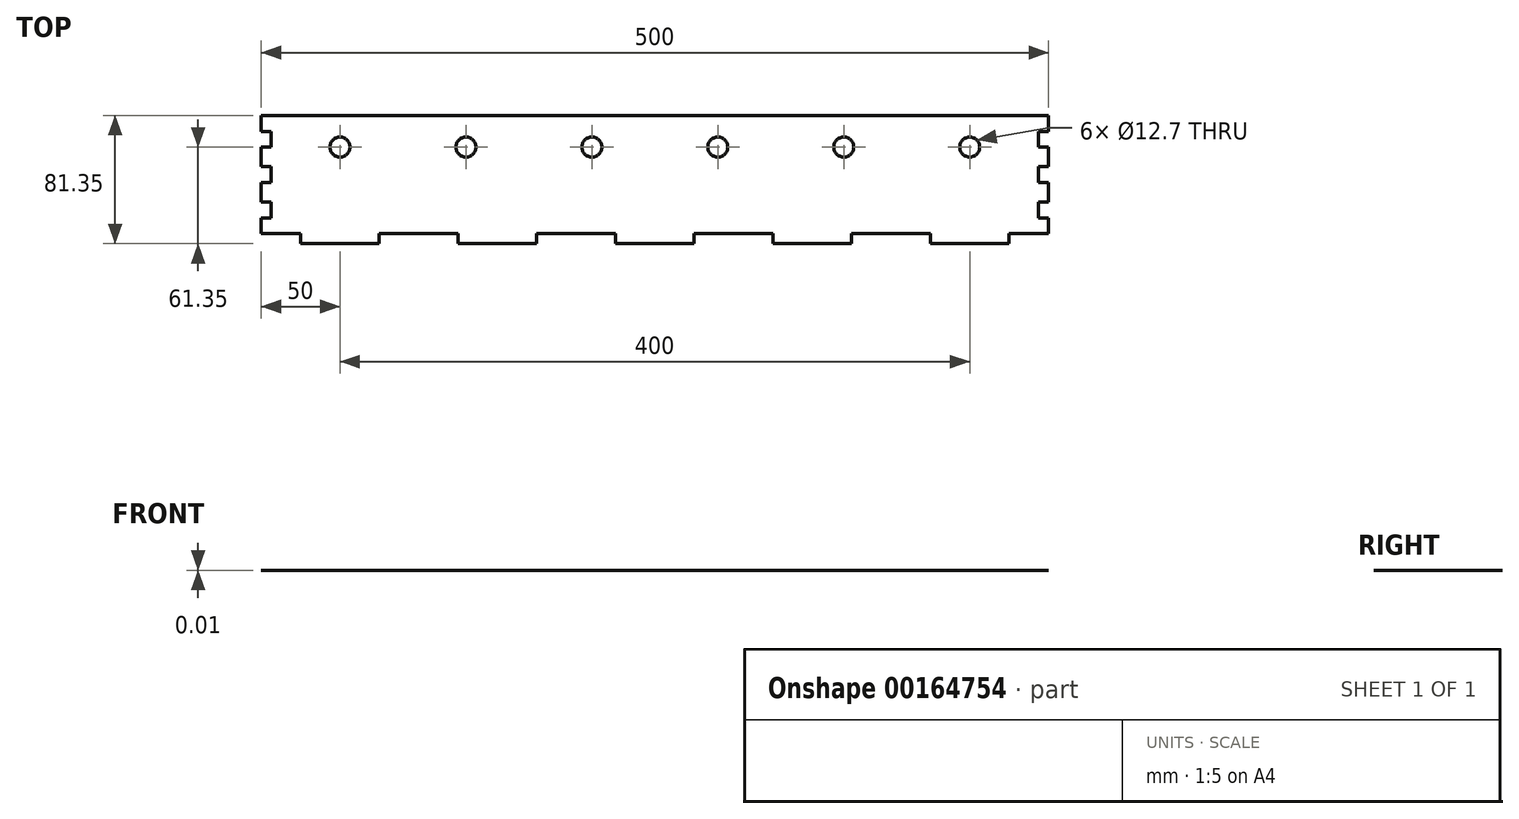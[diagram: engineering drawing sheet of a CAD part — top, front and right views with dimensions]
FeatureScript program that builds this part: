
annotation { "Feature Type Name" : "Feature", "Feature Type Description" : "" }
export const myFeature = defineFeature(function(context is Context, id is Id, definition is map)
    precondition{}
    {
        {
            var Q0;
            Q0=qCreatedBy(makeId("Top.planeOp"),FACE);
            var sketch = newSketch(context, id + "F0", { "sketchPlane" : qUnion([Q0])});
            skLineSegment(sketch, "E0.bottom", {"start": v(-250, 37.5) * mm, "end": v(250, 37.5) * mm});
            skLineSegment(sketch, "E0.top", {"start": v(-250, -37.5) * mm, "end": v(250, -37.5) * mm});
            skLineSegment(sketch, "E0.left", {"start": v(-250, 37.5) * mm, "end": v(-250, -37.5) * mm});
            skLineSegment(sketch, "E0.right", {"start": v(250, 37.5) * mm, "end": v(250, -37.5) * mm});
            skPoint(sketch, "E0.middle", {"position": v(0, 0) * mm});
            skSolve(sketch);
        }
        {
            var Q0;
            Q0=qSketchRegion(id+"F0",true);
            extrude(context, id + "F1", {"entities" : qUnion([Q0]), "depth" : 1 / 101.6 * mm});
        }
        {
            var Q0;
            Q0=makeQuery(id+"F1.opExtrude","CAP_FACE",FACE,{"disambiguationData":[OSD([sQuery(id+"F0.wireOp",EDGE,"E0.bottom"),sQuery(id+"F0.wireOp",EDGE,"E0.top"),sQuery(id+"F0.wireOp",EDGE,"E0.left"),sQuery(id+"F0.wireOp",EDGE,"E0.right")])],"isStart":false});
            var sketch = newSketch(context, id + "F2", { "sketchPlane" : qUnion([Q0])});
            skLineSegment(sketch, "E1.bottom", {"start": v(-225, 37.5) * mm, "end": v(-175, 37.5) * mm, "construction": true});
            skLineSegment(sketch, "E1.top", {"start": v(-225, 31.15) * mm, "end": v(-175, 31.15) * mm, "construction": true});
            skLineSegment(sketch, "E1.left", {"start": v(-225, 37.5) * mm, "end": v(-225, 31.15) * mm, "construction": true});
            skLineSegment(sketch, "E1.right", {"start": v(-175, 37.5) * mm, "end": v(-175, 31.15) * mm, "construction": true});
            skLineSegment(sketch, "E2.0.1.0", {"start": v(-225, -37.5) * mm, "end": v(-175, -37.5) * mm});
            skLineSegment(sketch, "E2.0.1.1", {"start": v(-225, -43.85) * mm, "end": v(-175, -43.85) * mm});
            skLineSegment(sketch, "E2.0.1.2", {"start": v(-225, -37.5) * mm, "end": v(-225, -43.85) * mm});
            skLineSegment(sketch, "E2.0.1.3", {"start": v(-175, -37.5) * mm, "end": v(-175, -43.85) * mm});
            skLineSegment(sketch, "E2.1.0.0", {"start": v(-125, 37.5) * mm, "end": v(-75, 37.5) * mm, "construction": true});
            skLineSegment(sketch, "E2.1.0.1", {"start": v(-125, 31.15) * mm, "end": v(-75, 31.15) * mm, "construction": true});
            skLineSegment(sketch, "E2.1.0.2", {"start": v(-125, 37.5) * mm, "end": v(-125, 31.15) * mm, "construction": true});
            skLineSegment(sketch, "E2.1.0.3", {"start": v(-75, 37.5) * mm, "end": v(-75, 31.15) * mm, "construction": true});
            skLineSegment(sketch, "E2.1.1.0", {"start": v(-125, -37.5) * mm, "end": v(-75, -37.5) * mm});
            skLineSegment(sketch, "E2.1.1.1", {"start": v(-125, -43.85) * mm, "end": v(-75, -43.85) * mm});
            skLineSegment(sketch, "E2.1.1.2", {"start": v(-125, -37.5) * mm, "end": v(-125, -43.85) * mm});
            skLineSegment(sketch, "E2.1.1.3", {"start": v(-75, -37.5) * mm, "end": v(-75, -43.85) * mm});
            skLineSegment(sketch, "E2.2.0.0", {"start": v(-25, 37.5) * mm, "end": v(25, 37.5) * mm, "construction": true});
            skLineSegment(sketch, "E2.2.0.1", {"start": v(-25, 31.15) * mm, "end": v(25, 31.15) * mm, "construction": true});
            skLineSegment(sketch, "E2.2.0.2", {"start": v(-25, 37.5) * mm, "end": v(-25, 31.15) * mm, "construction": true});
            skLineSegment(sketch, "E2.2.0.3", {"start": v(25, 37.5) * mm, "end": v(25, 31.15) * mm, "construction": true});
            skLineSegment(sketch, "E2.2.1.0", {"start": v(-25, -37.5) * mm, "end": v(25, -37.5) * mm});
            skLineSegment(sketch, "E2.2.1.1", {"start": v(-25, -43.85) * mm, "end": v(25, -43.85) * mm});
            skLineSegment(sketch, "E2.2.1.2", {"start": v(-25, -37.5) * mm, "end": v(-25, -43.85) * mm});
            skLineSegment(sketch, "E2.2.1.3", {"start": v(25, -37.5) * mm, "end": v(25, -43.85) * mm});
            skLineSegment(sketch, "E2.3.0.0", {"start": v(75, 37.5) * mm, "end": v(125, 37.5) * mm, "construction": true});
            skLineSegment(sketch, "E2.3.0.1", {"start": v(75, 31.15) * mm, "end": v(125, 31.15) * mm, "construction": true});
            skLineSegment(sketch, "E2.3.0.2", {"start": v(75, 37.5) * mm, "end": v(75, 31.15) * mm, "construction": true});
            skLineSegment(sketch, "E2.3.0.3", {"start": v(125, 37.5) * mm, "end": v(125, 31.15) * mm, "construction": true});
            skLineSegment(sketch, "E2.3.1.0", {"start": v(75, -37.5) * mm, "end": v(125, -37.5) * mm});
            skLineSegment(sketch, "E2.3.1.1", {"start": v(75, -43.85) * mm, "end": v(125, -43.85) * mm});
            skLineSegment(sketch, "E2.3.1.2", {"start": v(75, -37.5) * mm, "end": v(75, -43.85) * mm});
            skLineSegment(sketch, "E2.3.1.3", {"start": v(125, -37.5) * mm, "end": v(125, -43.85) * mm});
            skLineSegment(sketch, "E2.4.0.0", {"start": v(175, 37.5) * mm, "end": v(225, 37.5) * mm, "construction": true});
            skLineSegment(sketch, "E2.4.0.1", {"start": v(175, 31.15) * mm, "end": v(225, 31.15) * mm, "construction": true});
            skLineSegment(sketch, "E2.4.0.2", {"start": v(175, 37.5) * mm, "end": v(175, 31.15) * mm, "construction": true});
            skLineSegment(sketch, "E2.4.0.3", {"start": v(225, 37.5) * mm, "end": v(225, 31.15) * mm, "construction": true});
            skLineSegment(sketch, "E2.4.1.0", {"start": v(175, -37.5) * mm, "end": v(225, -37.5) * mm});
            skLineSegment(sketch, "E2.4.1.1", {"start": v(175, -43.85) * mm, "end": v(225, -43.85) * mm});
            skLineSegment(sketch, "E2.4.1.2", {"start": v(175, -37.5) * mm, "end": v(175, -43.85) * mm});
            skLineSegment(sketch, "E2.4.1.3", {"start": v(225, -37.5) * mm, "end": v(225, -43.85) * mm});
            skLineSegment(sketch, "E2.direction1", {"start": v(-225, 31.15) * mm, "end": v(-125, 31.15) * mm, "construction": true});
            skLineSegment(sketch, "E2.direction2", {"start": v(-225, 31.15) * mm, "end": v(-225, -43.85) * mm, "construction": true});
            skLineSegment(sketch, "E3.bottom", {"start": v(250, 27.5) * mm, "end": v(243.65, 27.5) * mm, "construction": true});
            skLineSegment(sketch, "E3.top", {"start": v(250, 17.5) * mm, "end": v(243.65, 17.5) * mm, "construction": true});
            skLineSegment(sketch, "E3.left", {"start": v(250, 27.5) * mm, "end": v(250, 17.5) * mm, "construction": true});
            skLineSegment(sketch, "E3.right", {"start": v(243.65, 27.5) * mm, "end": v(243.65, 17.5) * mm, "construction": true});
            skLineSegment(sketch, "E4.0.1.0", {"start": v(243.65, 5) * mm, "end": v(243.65, -5) * mm, "construction": true});
            skLineSegment(sketch, "E4.0.1.1", {"start": v(250, 5) * mm, "end": v(250, -5) * mm, "construction": true});
            skLineSegment(sketch, "E4.0.1.2", {"start": v(250, 5) * mm, "end": v(243.65, 5) * mm, "construction": true});
            skLineSegment(sketch, "E4.0.1.3", {"start": v(250, -5) * mm, "end": v(243.65, -5) * mm, "construction": true});
            skLineSegment(sketch, "E4.direction1", {"start": v(243.65, 17.5) * mm, "end": v(243.65, 17.5) * mm});
            skLineSegment(sketch, "E4.direction2", {"start": v(243.65, 17.5) * mm, "end": v(243.65, 5) * mm, "construction": true});
            skLineSegment(sketch, "E5.0.0.2", {"start": v(243.65, -17.5) * mm, "end": v(243.65, -27.5) * mm, "construction": true});
            skLineSegment(sketch, "E5.3.0.2", {"start": v(250, -17.5) * mm, "end": v(250, -27.5) * mm, "construction": true});
            skLineSegment(sketch, "E5.6.0.2", {"start": v(250, -17.5) * mm, "end": v(243.65, -17.5) * mm, "construction": true});
            skLineSegment(sketch, "E5.9.0.2", {"start": v(250, -27.5) * mm, "end": v(243.65, -27.5) * mm, "construction": true});
            skSolve(sketch);
        }
        {
            var Q0;
            Q0=qSketchRegion(id+"F2",true);
            var Q1;
            Q1=makeQuery(id+"F1.opExtrude","CAP_FACE",FACE,{"disambiguationData":[OSD([sQuery(id+"F0.wireOp",EDGE,"E0.bottom"),sQuery(id+"F0.wireOp",EDGE,"E0.top"),sQuery(id+"F0.wireOp",EDGE,"E0.left"),sQuery(id+"F0.wireOp",EDGE,"E0.right")])],"isStart":true});
            extrude(context, id + "F3", {"entities" : qUnion([Q0]), "operationType" : NewBodyOperationType.ADD, "endBound" : BoundingType.UP_TO_SURFACE, "oppositeDirection" : true, "endBoundEntityFace" : qUnion([Q1]), "depth" : 25 * mm});
        }
        {
            var Q0;
            Q0=makeQuery(id+"F3.boolean.opBoolean","MERGE",FACE,{"derivedFrom":[makeQuery(id+"F1.opExtrude","CAP_FACE",FACE,{"disambiguationData":[OSD([sQuery(id+"F0.wireOp",EDGE,"E0.bottom"),sQuery(id+"F0.wireOp",EDGE,"E0.top"),sQuery(id+"F0.wireOp",EDGE,"E0.left"),sQuery(id+"F0.wireOp",EDGE,"E0.right")])],"isStart":false}),makeQuery(id+"F3.opExtrude","CAP_FACE",FACE,{"disambiguationData":[OSD([sQuery(id+"F2.wireOp",EDGE,"E2.0.1.0"),sQuery(id+"F2.wireOp",EDGE,"E2.0.1.1"),sQuery(id+"F2.wireOp",EDGE,"E2.0.1.2"),sQuery(id+"F2.wireOp",EDGE,"E2.0.1.3")])],"isStart":true}),makeQuery(id+"F3.opExtrude","CAP_FACE",FACE,{"disambiguationData":[OSD([sQuery(id+"F2.wireOp",EDGE,"E2.1.1.0"),sQuery(id+"F2.wireOp",EDGE,"E2.1.1.1"),sQuery(id+"F2.wireOp",EDGE,"E2.1.1.2"),sQuery(id+"F2.wireOp",EDGE,"E2.1.1.3")])],"isStart":true}),makeQuery(id+"F3.opExtrude","CAP_FACE",FACE,{"disambiguationData":[OSD([sQuery(id+"F2.wireOp",EDGE,"E2.2.1.0"),sQuery(id+"F2.wireOp",EDGE,"E2.2.1.1"),sQuery(id+"F2.wireOp",EDGE,"E2.2.1.2"),sQuery(id+"F2.wireOp",EDGE,"E2.2.1.3")])],"isStart":true}),makeQuery(id+"F3.opExtrude","CAP_FACE",FACE,{"disambiguationData":[OSD([sQuery(id+"F2.wireOp",EDGE,"E2.3.1.0"),sQuery(id+"F2.wireOp",EDGE,"E2.3.1.1"),sQuery(id+"F2.wireOp",EDGE,"E2.3.1.2"),sQuery(id+"F2.wireOp",EDGE,"E2.3.1.3")])],"isStart":true}),makeQuery(id+"F3.opExtrude","CAP_FACE",FACE,{"disambiguationData":[OSD([sQuery(id+"F2.wireOp",EDGE,"E2.4.1.0"),sQuery(id+"F2.wireOp",EDGE,"E2.4.1.1"),sQuery(id+"F2.wireOp",EDGE,"E2.4.1.2"),sQuery(id+"F2.wireOp",EDGE,"E2.4.1.3")])],"isStart":true})]});
            var sketch = newSketch(context, id + "F4", { "sketchPlane" : qUnion([Q0])});
            skLineSegment(sketch, "E6", {"start": v(243.65, 27.5) * mm, "end": v(243.65, 17.5) * mm});
            skLineSegment(sketch, "E7", {"start": v(243.65, 17.5) * mm, "end": v(250, 17.5) * mm});
            skLineSegment(sketch, "E8", {"start": v(250, 17.5) * mm, "end": v(250, 27.5) * mm});
            skLineSegment(sketch, "E9", {"start": v(250, 27.5) * mm, "end": v(243.65, 27.5) * mm});
            skLineSegment(sketch, "E10.0.1.0", {"start": v(250, 5) * mm, "end": v(243.65, 5) * mm});
            skLineSegment(sketch, "E10.0.1.1", {"start": v(243.65, -5) * mm, "end": v(250, -5) * mm});
            skLineSegment(sketch, "E10.0.1.2", {"start": v(250, -5) * mm, "end": v(250, 5) * mm});
            skLineSegment(sketch, "E10.0.1.3", {"start": v(243.65, 5) * mm, "end": v(243.65, -5) * mm});
            skLineSegment(sketch, "E10.0.2.0", {"start": v(250, -17.5) * mm, "end": v(243.65, -17.5) * mm});
            skLineSegment(sketch, "E10.0.2.1", {"start": v(243.65, -27.5) * mm, "end": v(250, -27.5) * mm});
            skLineSegment(sketch, "E10.0.2.2", {"start": v(250, -27.5) * mm, "end": v(250, -17.5) * mm});
            skLineSegment(sketch, "E10.0.2.3", {"start": v(243.65, -17.5) * mm, "end": v(243.65, -27.5) * mm});
            skLineSegment(sketch, "E10.1.0.0", {"start": v(-243.65, 27.5) * mm, "end": v(-250, 27.5) * mm});
            skLineSegment(sketch, "E10.1.0.1", {"start": v(-250, 17.5) * mm, "end": v(-243.65, 17.5) * mm});
            skLineSegment(sketch, "E10.1.0.2", {"start": v(-243.65, 17.5) * mm, "end": v(-243.65, 27.5) * mm});
            skLineSegment(sketch, "E10.1.0.3", {"start": v(-250, 27.5) * mm, "end": v(-250, 17.5) * mm});
            skLineSegment(sketch, "E10.1.1.0", {"start": v(-243.65, 5) * mm, "end": v(-250, 5) * mm});
            skLineSegment(sketch, "E10.1.1.1", {"start": v(-250, -5) * mm, "end": v(-243.65, -5) * mm});
            skLineSegment(sketch, "E10.1.1.2", {"start": v(-243.65, -5) * mm, "end": v(-243.65, 5) * mm});
            skLineSegment(sketch, "E10.1.1.3", {"start": v(-250, 5) * mm, "end": v(-250, -5) * mm});
            skLineSegment(sketch, "E10.1.2.0", {"start": v(-243.65, -17.5) * mm, "end": v(-250, -17.5) * mm});
            skLineSegment(sketch, "E10.1.2.1", {"start": v(-250, -27.5) * mm, "end": v(-243.65, -27.5) * mm});
            skLineSegment(sketch, "E10.1.2.2", {"start": v(-243.65, -27.5) * mm, "end": v(-243.65, -17.5) * mm});
            skLineSegment(sketch, "E10.1.2.3", {"start": v(-250, -17.5) * mm, "end": v(-250, -27.5) * mm});
            skLineSegment(sketch, "E10.direction1", {"start": v(243.65, 17.5) * mm, "end": v(-250, 17.5) * mm, "construction": true});
            skLineSegment(sketch, "E10.direction2", {"start": v(243.65, 17.5) * mm, "end": v(243.65, -5) * mm, "construction": true});
            skSolve(sketch);
        }
        {
            var Q0;
            Q0 = qSketchRegion(id + "F4", true);
            extrude(context, id + "F5", {"entities" : qUnion([Q0]), "operationType" : NewBodyOperationType.REMOVE, "endBound" : BoundingType.THROUGH_ALL, "oppositeDirection" : true, "depth" : 25 * mm});
        }
        {
            var Q0;
            {var subQ2=sQuery(id+"F2.wireOp",EDGE,"E2.0.1.0");Q0=makeQuery(id+"F2.imprint","IMPRINT",FACE,{"disambiguationData":[TD([[makeQuery(id+"F2.imprint","IMPRINT",EDGE,{"derivedFrom":subQ2}),1.0]])]});}
            var sketch = newSketch(context, id + "F6", { "sketchPlane" : qUnion([Q0])});
            skCircle(sketch, "E11", {"center": v(-200, 17.5) * mm, "radius": 6.35 * mm});
            skLineSegment(sketch, "E12", {"start": v(-243.65, 17.5) * mm, "end": v(-200, 17.5) * mm, "construction": true});
            skCircle(sketch, "E13.1.0.0", {"center": v(-120, 17.5) * mm, "radius": 6.35 * mm});
            skCircle(sketch, "E13.2.0.0", {"center": v(-40, 17.5) * mm, "radius": 6.35 * mm});
            skCircle(sketch, "E13.3.0.0", {"center": v(40, 17.5) * mm, "radius": 6.35 * mm});
            skLineSegment(sketch, "E13.direction1", {"start": v(-200, 17.5) * mm, "end": v(-120, 17.5) * mm, "construction": true});
            skCircle(sketch, "E14.0.4.0", {"center": v(120, 17.5) * mm, "radius": 6.35 * mm});
            skCircle(sketch, "E14.0.5.0", {"center": v(200, 17.5) * mm, "radius": 6.35 * mm});
            skSolve(sketch);
        }
        {
            var Q0;
            Q0 = qSketchRegion(id + "F6", true);
            extrude(context, id + "F7", {"entities" : qUnion([Q0]), "operationType" : NewBodyOperationType.REMOVE, "oppositeDirection" : true, "depth" : 25 * mm});
        }
    });
